# Revit family: RN 81126 Optipress-Aquaplus-Übergang
name_source: partatom
category: Rohrformteile
units: mm (PartAtom-declared; Revit-internal decimal feet)

## family parameters
Arbeitsebenenbasiert = Nein
Beim Laden mit Abzugskörper schneiden = Nein
Bemaßung runder Anschluss = Durchmesser verwenden
Gemeinsam genutzt = Nein
Immer vertikal = Ja
Teiletyp = Verbindung

## types (2) — shared parameters
1.010.00.2 Blattnummer der Richtlinie = 29
1.010.00.3 Ausgabedatum (Monat) der Richtlinie = 201308
1.010.00.4 Herstellername = R. Nussbaum AG
1.010.00.5 Revisionsdatum der Datei = 20190521
1.010.00.6 Webadresse des Herstellers = http://www.nussbaum.ch
1.100.00.4 Produktbezeichnung = Versorgung
1.110.00.2 Index = 4
1.110.00.4 Produktbezeichnung = Optipress
1.960/3L.00.8 Link (URL) = https://www.nussbaum.ch
29.700.00.4 Produktname = Optipress-Aquaplus-Übergang, auf Stahlrohre
29.700.00.5 Produktkennung = 2
29.700.00.6 Querschnittsform = 1
29.700.00.7 Nennweitensystem = DN
29.700.00.8 Nenndrucksystem = PN
29.710.02.4 Nenndruck = 16
29.710.02.5 max. zul. Überdruck [hPa] = 1600
29.710.02.7 max. zul. Dauer-Betriebsdruck [hPa] = 1600
29.710.02.9 max. zul. Dauer-Betriebstemperatur [°C] = 95
Connector Visibility = Nein
EnclosingSpace Visibility = Nein
Hersteller = R. Nussbaum AG
URL = https://www.nussbaum.ch

## per-type parameters (varying)
| type | 1.800.00.3 TGA-Nummer | 1.800.00.4 Kommentarfeld | 1.810.00.3 Hersteller-Bestellnummer | 1.810.00.4 DATANORM-Nummer | 1.810.00.5 StLB-Nummer | 1.810.00.6 GTIN-Nummer | 29.710.02.10 Formstück-Gewicht [kg] | 29.710.02.3 Benennung | CONNECTOR0_DIAMETER_dX_0r | CONNECTOR0_dX_01 | CONNECTOR0_ref_dX | CONNECTOR1_DIAMETER_dX_0r | CONNECTOR1_dX_00 | CONNECTOR1_dX_01 | CONNECTOR1_ref_dX | Modell | R. Nussbaum AG 81126.25 de Visibility | R. Nussbaum AG 81126.26 de Visibility | Typenkommentare |
| DN=32x40 | 01900400000000000000000000000000000000000000000060000000000000000002 | 81126.26, Optipress-Aquaplus-Übergang, auf Stahlrohre, DN=32x40, L=112 | 81126.26 | 81126.26 | 267.216 | 7612945697561 | 0.984 | Optipress-Aquaplus-Übergang, auf Stahlrohre, DN=32x40, L=112 | 32 mm | 19 mm | 19 mm | 32 mm | 86 mm | 112 mm | 86 mm | 81126.26 | Nein | Ja | Optipress-Aquaplus-Übergang DN=32x40 |
| DN=25x32 | 01900400000000000000000000000000000000000000000060000000000000000001 | 81126.25, Optipress-Aquaplus-Übergang, auf Stahlrohre, DN=25x32, L=104 | 81126.25 | 81126.25 | 267.215 | 7612945697554 | 0.516 | Optipress-Aquaplus-Übergang, auf Stahlrohre, DN=25x32, L=104 | 25 mm  [stored 0.082021 ft] | 17 mm | 17 mm | 25 mm  [stored 0.082021 ft] | 80 mm | 104 mm | 80 mm | 81126.25 | Ja | Nein | Optipress-Aquaplus-Übergang DN=25x32 |

note: [stored X ft] marks values corroborated as IEEE doubles in the binary element streams (Revit-internal decimal feet)

## geometry (parser evidence)
native form markers: Sweep x2
no freeform markers — native parametric forms only
